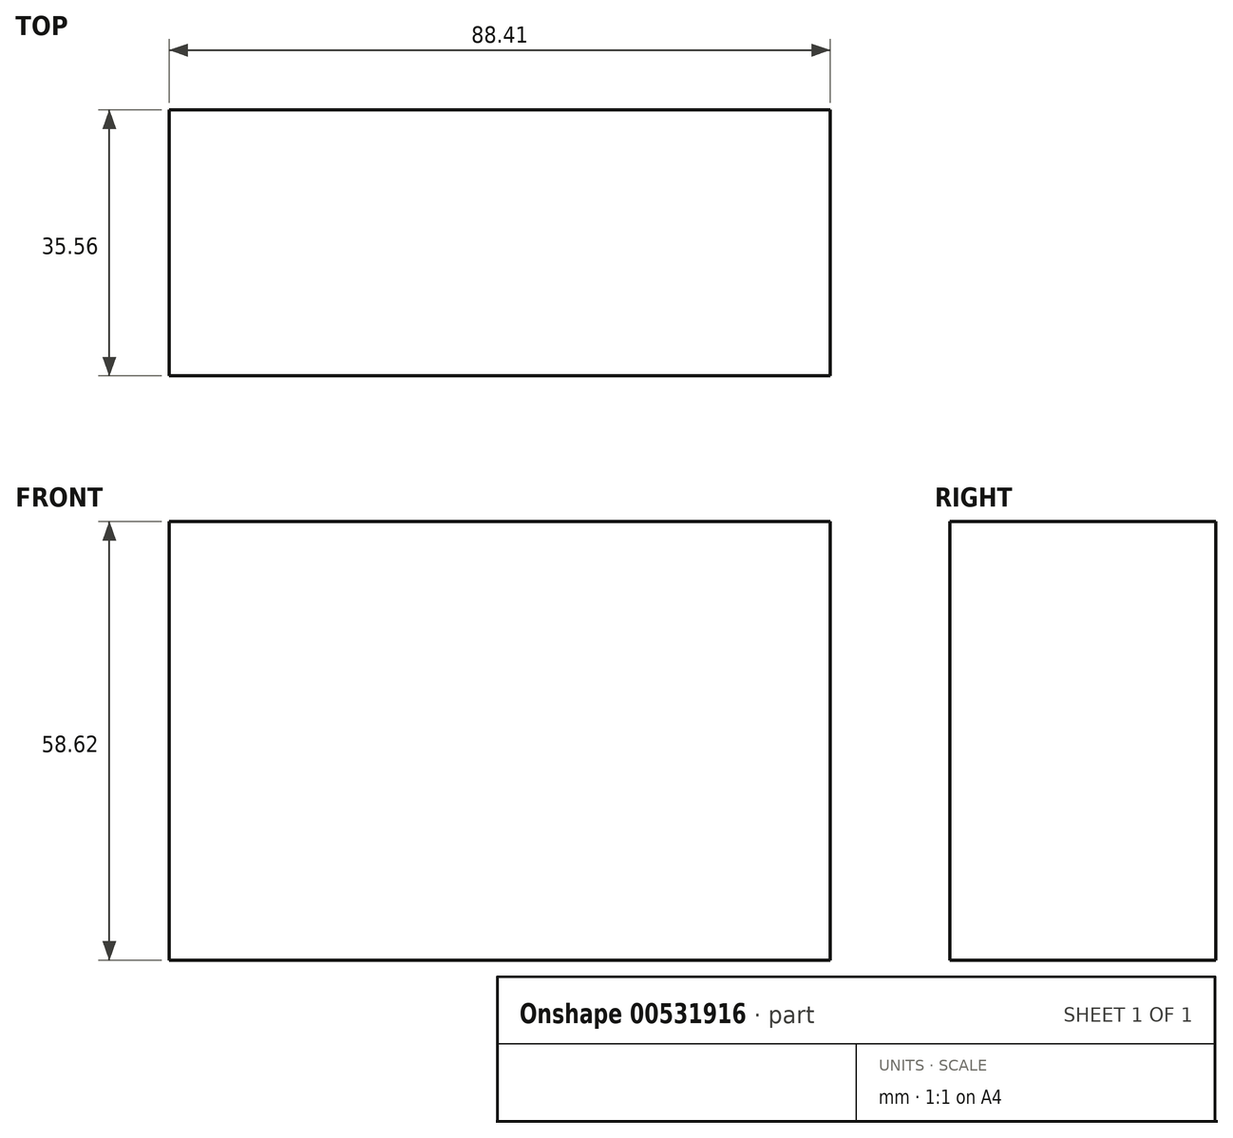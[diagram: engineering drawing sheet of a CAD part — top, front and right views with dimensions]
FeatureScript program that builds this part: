
annotation { "Feature Type Name" : "Feature", "Feature Type Description" : "" }
export const myFeature = defineFeature(function(context is Context, id is Id, definition is map)
    precondition{}
    {
        {
            var Q0;
            Q0=qCreatedBy(makeId("Front.planeOp"),FACE);
            var sketch = newSketch(context, id + "F0", { "sketchPlane" : qUnion([Q0])});
            skLineSegment(sketch, "E0.bottom", {"start": v(-42.96, 25.97) * mm, "end": v(45.45, 25.97) * mm});
            skLineSegment(sketch, "E0.top", {"start": v(-42.96, -32.65) * mm, "end": v(45.45, -32.65) * mm});
            skLineSegment(sketch, "E0.left", {"start": v(-42.96, 25.97) * mm, "end": v(-42.96, -32.65) * mm});
            skLineSegment(sketch, "E0.right", {"start": v(45.45, 25.97) * mm, "end": v(45.45, -32.65) * mm});
            skSolve(sketch);
        }
        {
            var Q0;
            Q0=makeQuery(id+"F0.imprint","IMPRINT",FACE,{"disambiguationData":[TD([[makeQuery(id+"F0.imprint","IMPRINT",EDGE,{"derivedFrom":sQuery(id+"F0.wireOp",EDGE,"E0.bottom")}),-1.0]])]});
            extrude(context, id + "F1", {"entities" : qUnion([Q0]), "oppositeDirection" : true, "depth" : 35.56 * mm, "offsetDistance" : 25.4 * mm});
        }
    });
